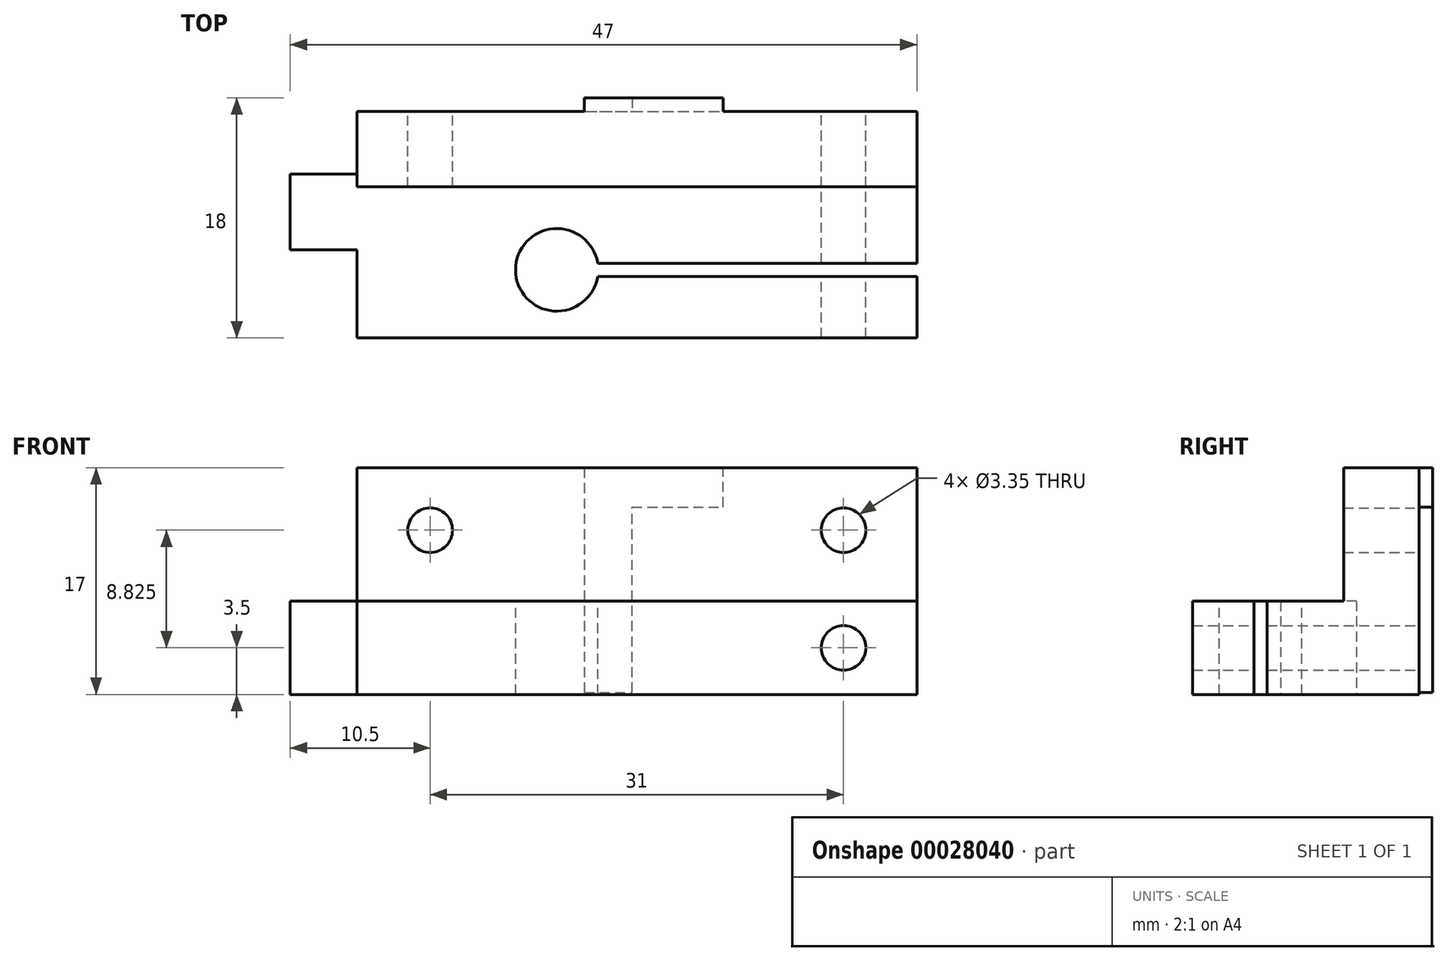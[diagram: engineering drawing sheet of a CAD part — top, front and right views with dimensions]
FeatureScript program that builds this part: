
annotation { "Feature Type Name" : "Feature", "Feature Type Description" : "" }
export const myFeature = defineFeature(function(context is Context, id is Id, definition is map)
    precondition{}
    {
        {
            var Q0;
            Q0=qCreatedBy(makeId("Top.planeOp"),FACE);
            var sketch = newSketch(context, id + "F0", { "sketchPlane" : qUnion([Q0])});
            skLineSegment(sketch, "E0.bottom", {"start": v(0, 0) * mm, "end": v(42, 0) * mm});
            skLineSegment(sketch, "E0.top", {"start": v(0, 17) * mm, "end": v(42, 17) * mm});
            skLineSegment(sketch, "E0.left", {"start": v(0, 0) * mm, "end": v(0, 17) * mm});
            skLineSegment(sketch, "E0.right", {"start": v(42, 0) * mm, "end": v(42, 17) * mm});
            skSolve(sketch);
        }
        {
            var Q0;
            Q0=qSketchRegion(id+"F0",true);
            extrude(context, id + "F1", {"entities" : qUnion([Q0]), "depth" : 7 * mm});
        }
        {
            var Q0;
            Q0=makeQuery(id+"F1.opExtrude","CAP_FACE",FACE,{"disambiguationData":[OSD([sQuery(id+"F0.wireOp",EDGE,"E0.bottom"),sQuery(id+"F0.wireOp",EDGE,"E0.top"),sQuery(id+"F0.wireOp",EDGE,"E0.left"),sQuery(id+"F0.wireOp",EDGE,"E0.right")])],"isStart":false});
            var sketch = newSketch(context, id + "F2", { "sketchPlane" : qUnion([Q0])});
            skCircle(sketch, "E1", {"center": v(15, 5.1) * mm, "radius": 3.1 * mm});
            skLineSegment(sketch, "E2", {"start": v(15, 5.1) * mm, "end": v(42, 5.1) * mm});
            skLineSegment(sketch, "E3", {"start": v(42, 5.1) * mm, "end": v(42, 4.6) * mm});
            skLineSegment(sketch, "E4", {"start": v(42, 4.6) * mm, "end": v(18.06, 4.6) * mm});
            skLineSegment(sketch, "E5", {"start": v(42, 5.1) * mm, "end": v(42, 5.6) * mm});
            skLineSegment(sketch, "E6", {"start": v(42, 5.6) * mm, "end": v(18.06, 5.6) * mm});
            skSolve(sketch);
        }
        {
            var Q0;
            Q0=makeQuery(id+"F1.opExtrude","SWEPT_FACE",FACE,{"disambiguationData":[OSD([sQuery(id+"F0.wireOp",EDGE,"E0.top")])]});
            var sketch = newSketch(context, id + "F3", { "sketchPlane" : qUnion([Q0])});
            skCircle(sketch, "E7", {"center": v(-36.5, 3.5) * mm, "radius": 1.68 * mm});
            skLineSegment(sketch, "E8", {"start": v(-36.5, 3.5) * mm, "end": v(-42, 3.5) * mm});
            skSolve(sketch);
        }
        {
            var Q0;
            Q0=qSketchRegion(id+"F3",true);
            extrude(context, id + "F4", {"entities" : qUnion([Q0]), "operationType" : NewBodyOperationType.REMOVE, "oppositeDirection" : true, "depth" : 25 * mm});
        }
        {
            var Q0;
            Q0=makeQuery(id+"F1.opExtrude","CAP_FACE",FACE,{"disambiguationData":[OSD([sQuery(id+"F0.wireOp",EDGE,"E0.bottom"),sQuery(id+"F0.wireOp",EDGE,"E0.top"),sQuery(id+"F0.wireOp",EDGE,"E0.left"),sQuery(id+"F0.wireOp",EDGE,"E0.right")])],"isStart":false});
            var sketch = newSketch(context, id + "F5", { "sketchPlane" : qUnion([Q0])});
            skLineSegment(sketch, "E9.bottom", {"start": v(0, 17) * mm, "end": v(42, 17) * mm});
            skLineSegment(sketch, "E9.top", {"start": v(0, 11.33) * mm, "end": v(42, 11.33) * mm});
            skLineSegment(sketch, "E9.left", {"start": v(0, 17) * mm, "end": v(0, 11.33) * mm});
            skLineSegment(sketch, "E9.right", {"start": v(42, 17) * mm, "end": v(42, 11.33) * mm});
            skSolve(sketch);
        }
        {
            var Q0;
            Q0=makeQuery(id+"F5.imprint","IMPRINT",FACE,{"disambiguationData":[TD([[makeQuery(id+"F5.imprint","IMPRINT",EDGE,{"derivedFrom":sQuery(id+"F5.wireOp",EDGE,"E9.bottom")}),-1.0]])]});
            extrude(context, id + "F6", {"entities" : qUnion([Q0]), "operationType" : NewBodyOperationType.ADD, "depth" : 10 * mm});
        }
        {
            var Q0;
            Q0=makeQuery(id+"F6.boolean.opBoolean","MERGE",FACE,{"derivedFrom":[makeQuery(id+"F1.opExtrude","SWEPT_FACE",FACE,{"disambiguationData":[OSD([sQuery(id+"F0.wireOp",EDGE,"E0.top")])]}),makeQuery(id+"F6.opExtrude","SWEPT_FACE",FACE,{"disambiguationData":[OSD([sQuery(id+"FFFDCbTcivKPk1C_1.wireOp",EDGE,"d29ae964-e38a-46b3-8ff4-cadffaec6662.bottom")])]})]});
            var sketch = newSketch(context, id + "F7", { "sketchPlane" : qUnion([Q0])});
            skPoint(sketch, "E10", {"position": v(-36.5, 3.5) * mm});
            skCircle(sketch, "E11", {"center": v(-36.5, 12.33) * mm, "radius": 1.68 * mm});
            skCircle(sketch, "E12", {"center": v(-5.5, 12.33) * mm, "radius": 1.68 * mm});
            skSolve(sketch);
        }
        {
            var Q0;
            Q0=qSketchRegion(id+"F7",true);
            extrude(context, id + "F8", {"entities" : qUnion([Q0]), "operationType" : NewBodyOperationType.REMOVE, "oppositeDirection" : true, "depth" : 25 * mm});
        }
        {
            var Q0;
            Q0=qSketchRegion(id+"F2",true);
            extrude(context, id + "F9", {"entities" : qUnion([Q0]), "operationType" : NewBodyOperationType.REMOVE, "oppositeDirection" : true, "depth" : 25 * mm});
        }
        {
            var Q0;
            Q0=makeQuery(id+"F6.boolean.opBoolean","MERGE",FACE,{"derivedFrom":[makeQuery(id+"F1.opExtrude","SWEPT_FACE",FACE,{"disambiguationData":[OSD([sQuery(id+"F0.wireOp",EDGE,"E0.top")])]}),makeQuery(id+"F6.opExtrude","SWEPT_FACE",FACE,{"disambiguationData":[OSD([sQuery(id+"F5.wireOp",EDGE,"E9.bottom")])]})]});
            var sketch = newSketch(context, id + "F10", { "sketchPlane" : qUnion([Q0])});
            skText(sketch, "E13", { "text": "L", "fontName": "OpenSans-Bold.ttf"});
            const initialGuessF10  = {"E13": [-0.01494, 0.017, -1, 0, 0.017]};
            skSetInitialGuess(sketch, initialGuessF10);
            skSolve(sketch);
        }
        {
            var Q0;
            Q0=qSketchRegion(id+"F10",true);
            extrude(context, id + "F11", {"entities" : qUnion([Q0]), "operationType" : NewBodyOperationType.ADD, "depth" : 1 * mm});
        }
        {
            var Q0;
            Q0=makeQuery(id+"F6.boolean.opBoolean","MERGE",FACE,{"derivedFrom":[makeQuery(id+"F1.opExtrude","SWEPT_FACE",FACE,{"disambiguationData":[OSD([sQuery(id+"F0.wireOp",EDGE,"E0.left")])]}),makeQuery(id+"F6.opExtrude","SWEPT_FACE",FACE,{"disambiguationData":[OSD([sQuery(id+"F5.wireOp",EDGE,"E9.left")])]})]});
            var sketch = newSketch(context, id + "F12", { "sketchPlane" : qUnion([Q0])});
            skLineSegment(sketch, "E14.bottom", {"start": v(-12.3, 7) * mm, "end": v(-6.6, 7) * mm});
            skLineSegment(sketch, "E14.top", {"start": v(-12.3, 0) * mm, "end": v(-6.6, 0) * mm});
            skLineSegment(sketch, "E14.left", {"start": v(-12.3, 7) * mm, "end": v(-12.3, 0) * mm});
            skLineSegment(sketch, "E14.right", {"start": v(-6.6, 7) * mm, "end": v(-6.6, 0) * mm});
            skSolve(sketch);
        }
        {
            var Q0;
            Q0=qSketchRegion(id+"F12",true);
            extrude(context, id + "F13", {"entities" : qUnion([Q0]), "operationType" : NewBodyOperationType.ADD, "depth" : 5 * mm});
        }
    });
